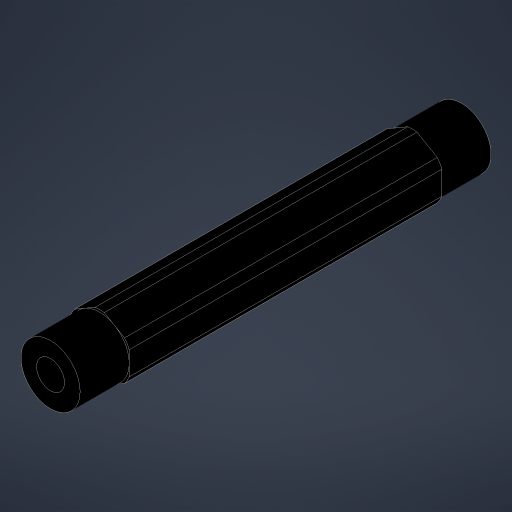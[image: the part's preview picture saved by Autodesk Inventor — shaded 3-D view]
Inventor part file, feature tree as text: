
AUTODESK INVENTOR PART (.ipt)
format: ipt  version: 2023.4 (Build 274418000, 418)  size: 249,856 bytes
history: native  units: in
note: dims shown in document units (in); Inventor stores cm internally (conversion verified against a paired STEP export)
features: extrude x3, projected_geometry x3, hole x1, mirror x1, sketch x1
ambient origin geometry x8: Origin, YZ Plane, XZ Plane, XY Plane, X Axis, Y Axis, Z Axis, Center Point
bodies: Solid1 (feature_tree)
feature tree (9):
  extrude  "Extrusion1"  Depth=0.375in
  hole  "Hole1"  [1 undecoded]
  extrude  "Extrusion3"  Depth=0.312in TaperAngle=0.0deg
  extrude  "Extrusion4"  Depth=0.375in
  mirror  "Mirror2"
  sketch  "Sketch5"  dims[d2=0.0in d9=0.625in d10=0.385in d11=0.25in d12=0.5635in d13=1.0in d14=0.8108in d16=0.7in d17=0.0in d18=0.0in d19=0.312in d20=0.0in d21=0.375in d22=0.5in d23=0.0344in d24=0.5in d25=0.0344in]
  projected_geometry  "Projected Loop2"
  projected_geometry  "Project Cut Edges1"
  projected_geometry  "Project Cut Edges2"
note: 1 required parameter value undecoded (feature->parameter linkage not recoverable at this tier; creation-order binding heuristic only, values carry confidence <= 0.55)
